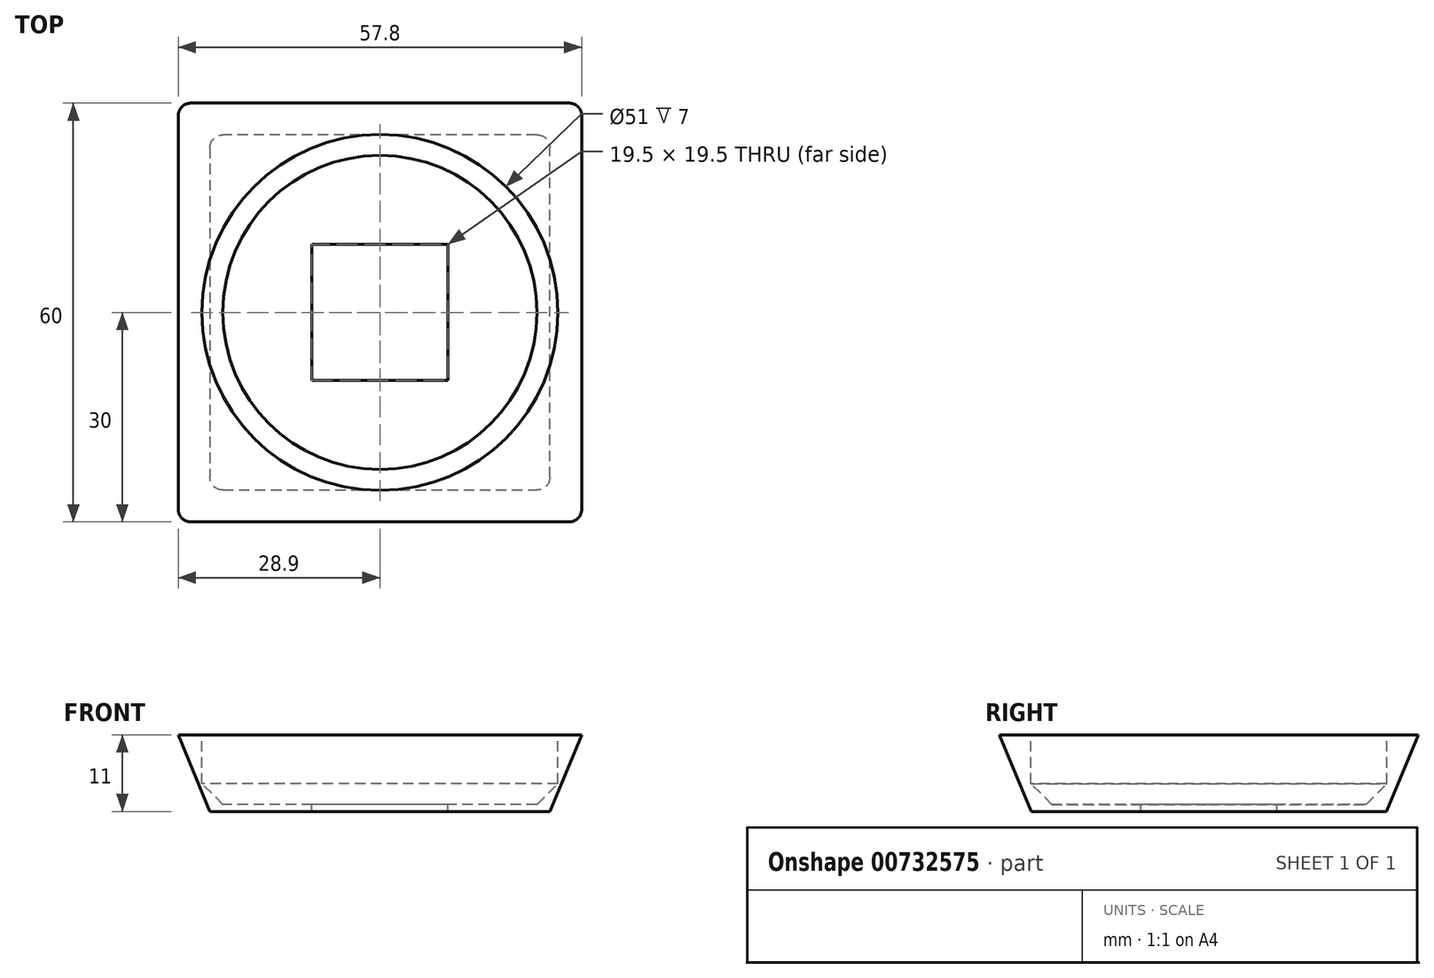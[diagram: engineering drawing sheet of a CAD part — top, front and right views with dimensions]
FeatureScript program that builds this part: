
annotation { "Feature Type Name" : "Feature", "Feature Type Description" : "" }
export const myFeature = defineFeature(function(context is Context, id is Id, definition is map)
    precondition{}
    {
        {
            assignVariable(context, id + "F0", {"name" : "Size", "anyValue" : 60});
        }
        {
            var Q0;
            Q0=qCreatedBy(makeId("Front.planeOp"),FACE);
            var sketch = newSketch(context, id + "F1", { "sketchPlane" : qUnion([Q0])});
            skLineSegment(sketch, "E0", {"start": v(0, 0) * mm, "end": v(-24.34, 0) * mm});
            skLineSegment(sketch, "E1", {"start": v(-24.34, 0) * mm, "end": v(-28.9, 0) * mm});
            skLineSegment(sketch, "E2", {"start": v(0, 0) * mm, "end": v(28.9, 0) * mm});
            skLineSegment(sketch, "E3", {"start": v(-24.34, 0) * mm, "end": v(-28.9, 11) * mm});
            skLineSegment(sketch, "E4", {"start": v(-28.9, 11) * mm, "end": v(28.9, 11) * mm});
            skLineSegment(sketch, "E5", {"start": v(-28.9, 11) * mm, "end": v(-28.9, 0) * mm});
            skLineSegment(sketch, "E6", {"start": v(-26, 4) * mm, "end": v(0, 4) * mm, "construction": true});
            skLineSegment(sketch, "E7", {"start": v(28.9, 11) * mm, "end": v(28.9, 0) * mm});
            skLineSegment(sketch, "E8", {"start": v(0, 11) * mm, "end": v(0, 4) * mm, "construction": true});
            skLineSegment(sketch, "E9", {"start": v(0, 4) * mm, "end": v(0, 0) * mm, "construction": true});
            skSolve(sketch);
        }
        {
            var Q0;
            Q0 = qSketchRegion(id + "F1", true);
            extrude(context, id + "F2", {"entities" : qUnion([Q0]), "endBound" : BoundingType.SYMMETRIC, "depth" : (getVariable(context, 'Size')) * mm, "offsetDistance" : 25 * mm});
        }
        {
            var Q0;
            Q0=makeQuery(id+"F1.imprint","IMPRINT",FACE,{"disambiguationData":[TD([[makeQuery(id+"F1.imprint","IMPRINT",EDGE,{"derivedFrom":sQuery(id+"F1.wireOp",EDGE,"E1")}),-1.0]])]});
            var Q1;
            Q1=makeQuery(id+"F2.opExtrude","SWEPT_EDGE",EDGE,{"disambiguationData":[OSD([sQuery(id+"F1.wireOp",EDGE,"E3"),sQuery(id+"F1.wireOp",EDGE,"E4"),sQuery(id+"F1.wireOp",EDGE,"E5")])]});
            var Q2;
            Q2=makeQuery(id+"F2.opExtrude","CAP_EDGE",EDGE,{"disambiguationData":[OSD([sQuery(id+"F1.wireOp",EDGE,"E4")])],"isStart":false});
            var Q3;
            Q3=makeQuery(id+"F2.opExtrude","SWEPT_EDGE",EDGE,{"disambiguationData":[OSD([sQuery(id+"F1.wireOp",EDGE,"E4"),sQuery(id+"F1.wireOp",EDGE,"2okiPtOC-y94u-vAih-ocOy-O6CLRNbMBZyq")])]});
            var Q4;
            Q4=makeQuery(id+"F2.opExtrude","CAP_EDGE",EDGE,{"disambiguationData":[OSD([sQuery(id+"F1.wireOp",EDGE,"E4")])],"isStart":true});
            sweep(context, id + "F3", {"operationType" : NewBodyOperationType.REMOVE, "profiles" : qUnion([Q0]), "path" : qUnion([Q1, Q2, Q3, Q4])});
        }
        {
            var Q0;
            Q0=makeQuery(id+"F2.opExtrude","SWEPT_FACE",FACE,{"disambiguationData":[OSD([sQuery(id+"F1.wireOp",EDGE,"E4")])]});
            var sketch = newSketch(context, id + "F4", { "sketchPlane" : qUnion([Q0])});
            skCircle(sketch, "E10", {"center": v(0, 0) * mm, "radius": 25.5 * mm});
            skLineSegment(sketch, "E11", {"start": v(0, 0) * mm, "end": v(25.5, 0) * mm, "construction": true});
            skSolve(sketch);
        }
        {
            var Q0;
            Q0=makeQuery(id+"F4.imprint","IMPRINT",FACE,{"disambiguationData":[TD([[makeQuery(id+"F4.imprint","IMPRINT",EDGE,{"derivedFrom":sQuery(id+"F4.wireOp",EDGE,"E10")}),1.0]])]});
            var Q1;
            Q1=sQuery(id+"F4.wireOp",EDGE,"E10");
            extrude(context, id + "F5", {"entities" : qUnion([Q0]), "operationType" : NewBodyOperationType.REMOVE, "surfaceEntities" : qUnion([Q1]), "oppositeDirection" : true, "depth" : 7 * mm, "offsetDistance" : 25 * mm});
        }
        {
            var Q0;
            Q0=makeQuery(id+"F5.boolean.opBoolean","COPY",FACE,{"derivedFrom":makeQuery(id+"F5.opExtrude","CAP_FACE",FACE,{"disambiguationData":[OSD([sQuery(id+"F4.wireOp",EDGE,"E10")])],"isStart":false})});
            extrude(context, id + "F6", {"entities" : qUnion([Q0]), "operationType" : NewBodyOperationType.REMOVE, "oppositeDirection" : true, "depth" : 3 * mm, "offsetDistance" : 25 * mm, "hasDraft" : true, "draftAngle" : 45 * degree, "draftPullDirection" : true});
        }
        {
            var Q0;
            Q0=makeQuery(id+"F6.boolean.opBoolean","COPY",FACE,{"derivedFrom":makeQuery(id+"F6.opExtrude","CAP_FACE",FACE,{"disambiguationData":[OSD([sQuery(id+"F4.wireOp",EDGE,"E10")])],"isStart":false})});
            var sketch = newSketch(context, id + "F7", { "sketchPlane" : qUnion([Q0])});
            skLineSegment(sketch, "E12.bottom", {"start": v(9.75, 9.75) * mm, "end": v(-9.75, 9.75) * mm});
            skLineSegment(sketch, "E12.top", {"start": v(9.75, -9.75) * mm, "end": v(-9.75, -9.75) * mm});
            skLineSegment(sketch, "E12.left", {"start": v(9.75, 9.75) * mm, "end": v(9.75, -9.75) * mm});
            skLineSegment(sketch, "E12.right", {"start": v(-9.75, 9.75) * mm, "end": v(-9.75, -9.75) * mm});
            skPoint(sketch, "E12.middle", {"position": v(0, 0) * mm});
            skSolve(sketch);
        }
        {
            var Q0;
            Q0=makeQuery(id+"F7.imprint","IMPRINT",FACE,{"disambiguationData":[TD([[makeQuery(id+"F7.imprint","IMPRINT",EDGE,{"derivedFrom":sQuery(id+"F7.wireOp",EDGE,"E12.bottom")}),1.0]])]});
            extrude(context, id + "F8", {"entities" : qUnion([Q0]), "operationType" : NewBodyOperationType.REMOVE, "oppositeDirection" : true, "depth" : 25 * mm, "offsetDistance" : 25 * mm});
        }
        {
            var Q0;
            {var subQ0=sQuery(id+"F1.wireOp",EDGE,"E4");var subQ1=sQuery(id+"F1.wireOp",EDGE,"E1");var subQ2=sQuery(id+"F1.wireOp",EDGE,"E0");var subQ3=sQuery(id+"F1.wireOp",EDGE,"PbRBcQyH-Xp2n-kDln-TprN-lvDJ9cFtrjTt");Q0=makeQuery(id+"F3.boolean.opBoolean","COPY",EDGE,{"derivedFrom":makeQuery(id+"F3.opSweep","SWEPT_EDGE",EDGE,{"disambiguationData":[OSD([subQ3,subQ2,subQ1,subQ0]),TDD([makeQuery(id+"F1.imprint","INTERSECT",VERTEX,{"derivedFrom":[subQ3,subQ2,subQ1]}),makeQuery(id+"F2.opExtrude","CAP_EDGE",EDGE,{"disambiguationData":[OSD([subQ0])],"isStart":false})])]})});}
            var Q1;
            Q1=makeQuery(id+"F3.boolean.opBoolean","COPY",EDGE,{"derivedFrom":makeQuery(id+"F3.opSweep","SWEPT_EDGE",EDGE,{"disambiguationData":[OSD([sQuery(id+"F1.wireOp",EDGE,"PbRBcQyH-Xp2n-kDln-TprN-lvDJ9cFtrjTt"),sQuery(id+"F1.wireOp",EDGE,"E0"),sQuery(id+"F1.wireOp",EDGE,"E1"),sQuery(id+"F1.wireOp",EDGE,"E4"),sQuery(id+"F1.wireOp",EDGE,"HmiGZg7Y-uqyB-Bz3N-8KUP-1Etw4MERJo5Z")])]})});
            var Q2;
            {var subQ0=sQuery(id+"F1.wireOp",EDGE,"E4");var subQ1=sQuery(id+"F1.wireOp",EDGE,"E1");var subQ2=sQuery(id+"F1.wireOp",EDGE,"E0");var subQ3=sQuery(id+"F1.wireOp",EDGE,"PbRBcQyH-Xp2n-kDln-TprN-lvDJ9cFtrjTt");Q2=makeQuery(id+"F3.boolean.opBoolean","COPY",EDGE,{"derivedFrom":makeQuery(id+"F3.opSweep","SWEPT_EDGE",EDGE,{"disambiguationData":[OSD([subQ3,subQ2,subQ1,subQ0]),TDD([makeQuery(id+"F1.imprint","INTERSECT",VERTEX,{"derivedFrom":[subQ3,subQ2,subQ1]}),makeQuery(id+"F2.opExtrude","CAP_EDGE",EDGE,{"disambiguationData":[OSD([subQ0])],"isStart":true})])]})});}
            var Q3;
            Q3=makeQuery(id+"F3.boolean.opBoolean","COPY",EDGE,{"derivedFrom":makeQuery(id+"F3.opSweep","SWEPT_EDGE",EDGE,{"disambiguationData":[OSD([sQuery(id+"F1.wireOp",EDGE,"PbRBcQyH-Xp2n-kDln-TprN-lvDJ9cFtrjTt"),sQuery(id+"F1.wireOp",EDGE,"E0"),sQuery(id+"F1.wireOp",EDGE,"E1"),sQuery(id+"F1.wireOp",EDGE,"E3"),sQuery(id+"F1.wireOp",EDGE,"E4"),sQuery(id+"F1.wireOp",EDGE,"E5")])]})});
            var Q4;
            Q4=makeQuery(id+"F3.boolean.opBoolean","COPY",EDGE,{"derivedFrom":makeQuery(id+"F3.opSweep","MID_CAP_EDGE",EDGE,{"disambiguationData":[OSD([sQuery(id+"F1.wireOp",EDGE,"PbRBcQyH-Xp2n-kDln-TprN-lvDJ9cFtrjTt"),sQuery(id+"F1.wireOp",EDGE,"E3"),sQuery(id+"F1.wireOp",EDGE,"E4"),sQuery(id+"F1.wireOp",EDGE,"E5")])],"capPos":3.0})});
            var Q5;
            Q5=makeQuery(id+"F3.boolean.opBoolean","COPY",EDGE,{"derivedFrom":makeQuery(id+"F3.opSweep","MID_CAP_EDGE",EDGE,{"disambiguationData":[OSD([sQuery(id+"F1.wireOp",EDGE,"PbRBcQyH-Xp2n-kDln-TprN-lvDJ9cFtrjTt"),sQuery(id+"F1.wireOp",EDGE,"E3"),sQuery(id+"F1.wireOp",EDGE,"E4"),sQuery(id+"F1.wireOp",EDGE,"HmiGZg7Y-uqyB-Bz3N-8KUP-1Etw4MERJo5Z")])],"capPos":2.0})});
            var Q6;
            Q6=makeQuery(id+"F3.boolean.opBoolean","COPY",EDGE,{"derivedFrom":makeQuery(id+"F3.opSweep","MID_CAP_EDGE",EDGE,{"disambiguationData":[OSD([sQuery(id+"F1.wireOp",EDGE,"PbRBcQyH-Xp2n-kDln-TprN-lvDJ9cFtrjTt"),sQuery(id+"F1.wireOp",EDGE,"E3"),sQuery(id+"F1.wireOp",EDGE,"E4"),sQuery(id+"F1.wireOp",EDGE,"HmiGZg7Y-uqyB-Bz3N-8KUP-1Etw4MERJo5Z")])],"capPos":1.0})});
            var Q7;
            Q7=makeQuery(id+"F3.boolean.opBoolean","COPY",EDGE,{"derivedFrom":makeQuery(id+"F3.opSweep","CAP_EDGE",EDGE,{"disambiguationData":[OSD([sQuery(id+"F1.wireOp",EDGE,"PbRBcQyH-Xp2n-kDln-TprN-lvDJ9cFtrjTt"),sQuery(id+"F1.wireOp",EDGE,"E3"),sQuery(id+"F1.wireOp",EDGE,"E4"),sQuery(id+"F1.wireOp",EDGE,"E5")])],"isStart":true})});
            fillet(context, id + "F9", {"entities" : qUnion([Q0, Q1, Q2, Q3, Q4, Q5, Q6, Q7]), "radius" : 2 * mm, "tangentPropagation" : true, "allowEdgeOverflow" : false});
        }
    });
